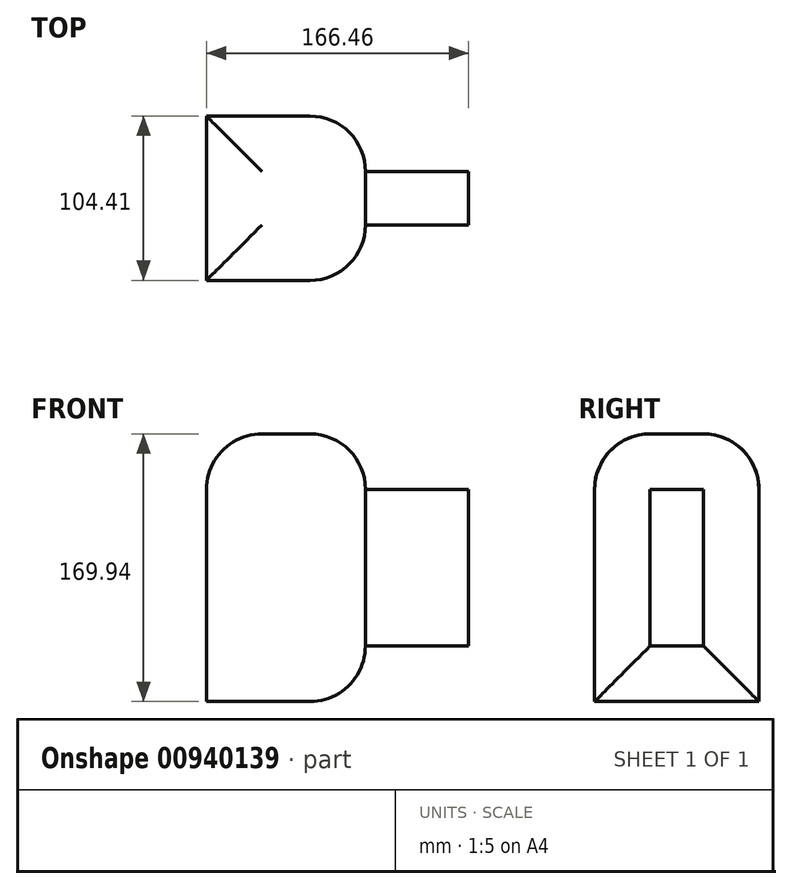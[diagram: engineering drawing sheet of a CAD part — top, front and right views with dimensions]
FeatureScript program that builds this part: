
annotation { "Feature Type Name" : "Feature", "Feature Type Description" : "" }
export const myFeature = defineFeature(function(context is Context, id is Id, definition is map)
    precondition{}
    {
        {
            var Q0;
            Q0=qCreatedBy(makeId("Front.planeOp"),FACE);
            var sketch = newSketch(context, id + "F0", { "sketchPlane" : qUnion([Q0])});
            skLineSegment(sketch, "E0.bottom", {"start": v(-48.5, -64.04) * mm, "end": v(52.45, -64.04) * mm});
            skLineSegment(sketch, "E0.top", {"start": v(-48.5, 105.9) * mm, "end": v(52.45, 105.9) * mm});
            skLineSegment(sketch, "E0.left", {"start": v(-48.5, -64.04) * mm, "end": v(-48.5, 105.9) * mm});
            skLineSegment(sketch, "E0.right", {"start": v(52.45, -64.04) * mm, "end": v(52.45, 105.9) * mm});
            skSolve(sketch);
        }
        {
            var Q0;
            Q0=makeQuery(id+"F0.imprint","IMPRINT",FACE,{"disambiguationData":[TD([[makeQuery(id+"F0.imprint","IMPRINT",EDGE,{"derivedFrom":sQuery(id+"F0.wireOp",EDGE,"E0.bottom")}),1.0]])]});
            var sketch = newSketch(context, id + "F1", { "sketchPlane" : qUnion([Q0])});
            skSolve(sketch);
        }
        {
            var Q0;
            Q0=makeQuery(id+"F1.imprint","IMPRINT",FACE,{"disambiguationData":[TD([[makeQuery(id+"F1.imprint","IMPRINT",EDGE,{"derivedFrom":makeQuery(id+"F0.imprint","IMPRINT",EDGE,{"derivedFrom":sQuery(id+"F0.wireOp",EDGE,"E0.bottom")})}),1.0]])]});
            extrude(context, id + "F2", {"entities" : qUnion([Q0]), "depth" : 104.4 * mm, "offsetDistance" : 25.4 * mm});
        }
        {
            var Q0;
            Q0=makeQuery(id+"F2.opExtrude","SWEPT_FACE",FACE,{"disambiguationData":[OSD([sQuery(id+"F0.wireOp",EDGE,"E0.top")])]});
            var Q1;
            Q1=makeQuery(id+"F2.opExtrude","SWEPT_FACE",FACE,{"disambiguationData":[OSD([sQuery(id+"F0.wireOp",EDGE,"E0.right")])]});
            fillet(context, id + "F3", {"entities" : qUnion([Q0, Q1]), "radius" : 35.23 * mm, "tangentPropagation" : true, "allowEdgeOverflow" : false});
        }
        {
            var Q0;
            Q0=makeQuery(id+"F2.opExtrude","SWEPT_FACE",FACE,{"disambiguationData":[OSD([sQuery(id+"F0.wireOp",EDGE,"E0.right")])]});
            extrude(context, id + "F4", {"entities" : qUnion([Q0]), "operationType" : NewBodyOperationType.ADD, "depth" : 65.5 * mm, "offsetDistance" : 25.4 * mm});
        }
    });
